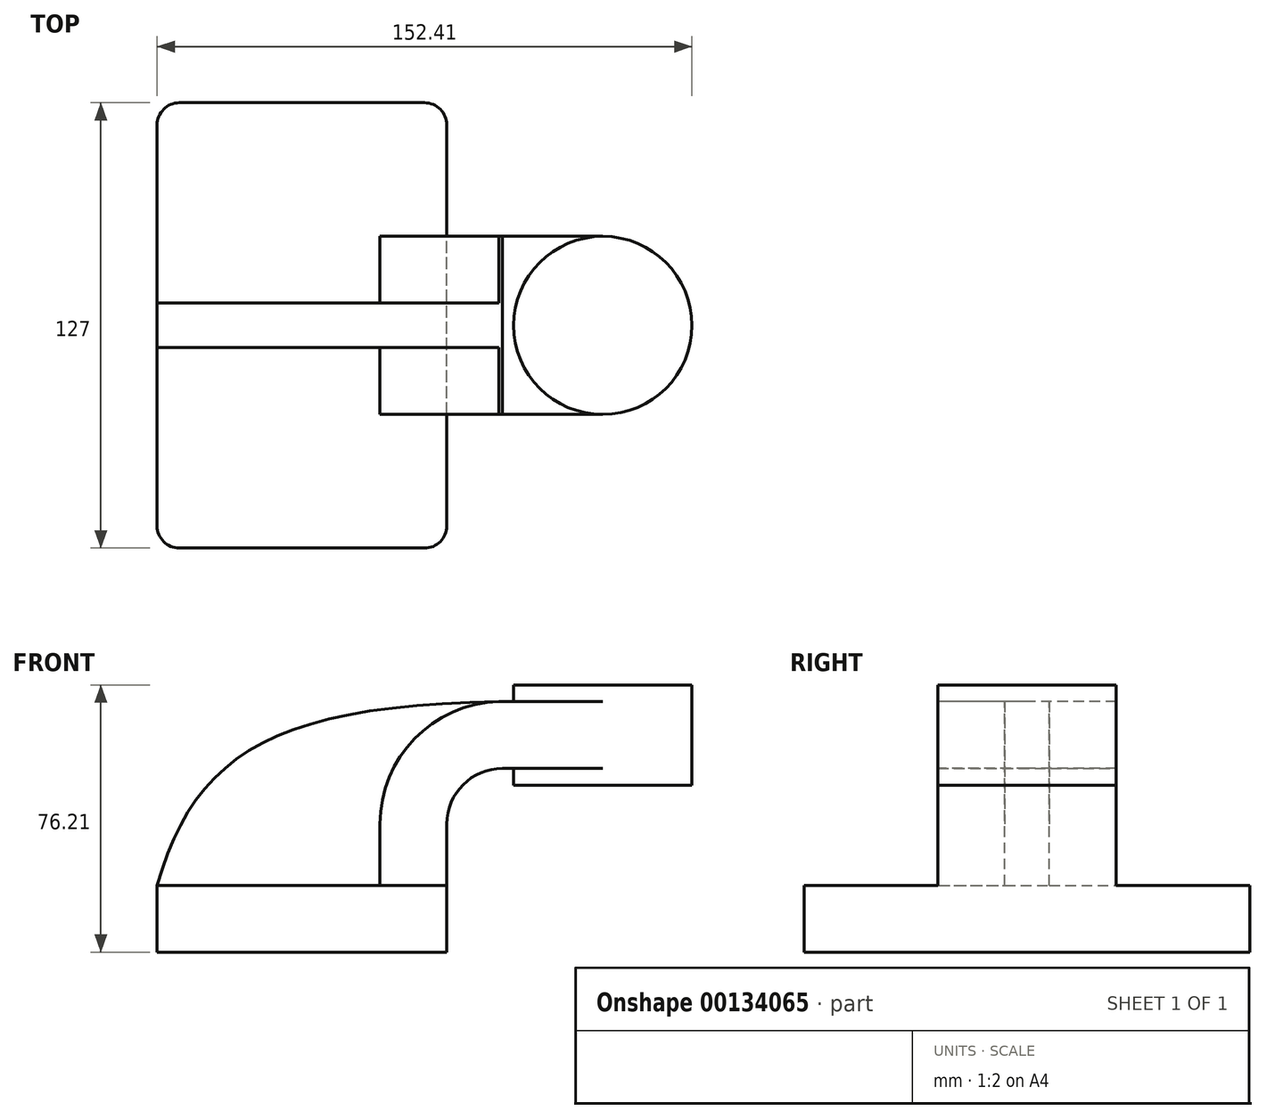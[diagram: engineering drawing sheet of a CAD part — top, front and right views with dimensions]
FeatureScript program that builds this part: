
annotation { "Feature Type Name" : "Feature", "Feature Type Description" : "" }
export const myFeature = defineFeature(function(context is Context, id is Id, definition is map)
    precondition{}
    {
        {
            var Q0;
            Q0=qCreatedBy(makeId("Front.planeOp"),FACE);
            var sketch = newSketch(context, id + "F0", { "sketchPlane" : qUnion([Q0])});
            skLineSegment(sketch, "E0.bottom", {"start": v(41.27, 9.53) * mm, "end": v(-41.28, 9.53) * mm});
            skLineSegment(sketch, "E0.top", {"start": v(41.28, -9.52) * mm, "end": v(-41.27, -9.52) * mm});
            skLineSegment(sketch, "E0.left", {"start": v(41.27, 9.53) * mm, "end": v(41.28, -9.52) * mm});
            skLineSegment(sketch, "E0.right", {"start": v(-41.28, 9.53) * mm, "end": v(-41.27, -9.52) * mm});
            skPoint(sketch, "E0.middle", {"position": v(0, 0) * mm});
            skLineSegment(sketch, "E1.bottom", {"start": v(111.12, 38.1) * mm, "end": v(60.32, 38.1) * mm});
            skLineSegment(sketch, "E1.top", {"start": v(111.12, 66.68) * mm, "end": v(60.32, 66.68) * mm});
            skLineSegment(sketch, "E1.left", {"start": v(111.12, 38.1) * mm, "end": v(111.12, 66.68) * mm});
            skLineSegment(sketch, "E1.right", {"start": v(60.32, 38.1) * mm, "end": v(60.32, 66.68) * mm});
            skPoint(sketch, "E1.middle", {"position": v(85.72, 52.39) * mm});
            skLineSegment(sketch, "E2", {"start": v(41.27, 9.53) * mm, "end": v(41.27, 26.99) * mm});
            skArc(sketch, "E3", {"start": v(41.27, 26.99) * mm, "mid": v(45.92, 38.21) * mm, "end": v(57.15, 42.86) * mm});
            skLineSegment(sketch, "E4", {"start": v(57.15, 42.86) * mm, "end": v(85.72, 42.86) * mm});
            skLineSegment(sketch, "E5.0", {"start": v(57.15, 61.91) * mm, "end": v(85.72, 61.91) * mm});
            skArc(sketch, "E5.1", {"start": v(22.22, 26.99) * mm, "mid": v(32.45, 51.68) * mm, "end": v(57.15, 61.91) * mm});
            skLineSegment(sketch, "E5.2", {"start": v(22.22, 9.53) * mm, "end": v(22.22, 26.99) * mm});
            skLineSegment(sketch, "E6", {"start": v(85.72, 38.1) * mm, "end": v(85.72, 42.86) * mm});
            skLineSegment(sketch, "E7", {"start": v(85.72, 42.86) * mm, "end": v(85.72, 52.39) * mm});
            skFitSpline(sketch, "E8", {"points": [v(-41.27, 9.52) * mm, v(57.15, 61.91) * mm], "startDerivative": vector(31.73, 110.33) * mm, "endDerivative": vector(198.85, 2.68) * mm});
            skLineSegment(sketch, "E9", {"start": v(85.72, 52.39) * mm, "end": v(85.72, 66.68) * mm});
            skSolve(sketch);
        }
        {
            var Q0;
            Q0=makeQuery(id+"F0.imprint","IMPRINT",FACE,{"disambiguationData":[TD([[makeQuery(id+"F0.imprint","IMPRINT",EDGE,{"derivedFrom":sQuery(id+"F0.wireOp",EDGE,"E0.bottom")}),1.0]])]});
            extrude(context, id + "F1", {"entities" : qUnion([Q0]), "endBound" : BoundingType.SYMMETRIC, "depth" : 127 * mm});
        }
        {
            var Q0;
            {var subQ0=sQuery(id+"F0.wireOp",EDGE,"E7");Q0=makeQuery(id+"F0.imprint","IMPRINT",FACE,{"disambiguationData":[TD([[makeQuery(id+"F0.imprint","IMPRINT",EDGE,{"derivedFrom":subQ0}),1.0]])]});}
            var Q1;
            {var subQ6=sQuery(id+"F0.wireOp",EDGE,"E2");Q1=makeQuery(id+"F0.imprint","IMPRINT",FACE,{"disambiguationData":[TD([[makeQuery(id+"F0.imprint","IMPRINT",EDGE,{"derivedFrom":subQ6}),1.0]])]});}
            extrude(context, id + "F2", {"entities" : qUnion([Q0, Q1]), "operationType" : NewBodyOperationType.ADD, "endBound" : BoundingType.SYMMETRIC, "depth" : 50.8 * mm});
        }
        {
            var Q0;
            {var subQ3=sQuery(id+"F0.wireOp",EDGE,"E5.2");Q0=makeQuery(id+"F0.imprint","IMPRINT",FACE,{"disambiguationData":[TD([[makeQuery(id+"F0.imprint","IMPRINT",EDGE,{"derivedFrom":subQ3}),1.0]])]});}
            extrude(context, id + "F3", {"entities" : qUnion([Q0]), "operationType" : NewBodyOperationType.ADD, "endBound" : BoundingType.SYMMETRIC, "depth" : 12.7 * mm});
        }
        {
            var Q0;
            {var subQ0=sQuery(id+"F0.wireOp",EDGE,"E1.left");Q0=makeQuery(id+"F0.imprint","IMPRINT",FACE,{"disambiguationData":[TD([[makeQuery(id+"F0.imprint","IMPRINT",EDGE,{"derivedFrom":subQ0}),1.0]])]});}
            var Q1;
            Q1=sQuery(id+"F0.wireOp",EDGE,"E9");
            revolve(context, id + "F4", {"operationType" : NewBodyOperationType.ADD, "entities" : qUnion([Q0]), "axis" : qUnion([Q1]), "revolveType" : RevolveType.FULL});
        }
        {
            var Q0;
            Q0=makeQuery(id+"F1.opExtrude","CAP_EDGE",EDGE,{"disambiguationData":[OSD([sQuery(id+"F0.wireOp",EDGE,"E0.left")])],"isStart":false});
            var Q1;
            Q1=makeQuery(id+"F1.opExtrude","CAP_EDGE",EDGE,{"disambiguationData":[OSD([sQuery(id+"F0.wireOp",EDGE,"E0.right")])],"isStart":false});
            var Q2;
            Q2=makeQuery(id+"F1.opExtrude","CAP_EDGE",EDGE,{"disambiguationData":[OSD([sQuery(id+"F0.wireOp",EDGE,"E0.left")])],"isStart":true});
            var Q3;
            Q3=makeQuery(id+"F1.opExtrude","CAP_EDGE",EDGE,{"disambiguationData":[OSD([sQuery(id+"F0.wireOp",EDGE,"E0.right")])],"isStart":true});
            fillet(context, id + "F5", {"entities" : qUnion([Q0, Q1, Q2, Q3]), "radius" : 6.35 * mm, "tangentPropagation" : true, "allowEdgeOverflow" : false});
        }
    });
